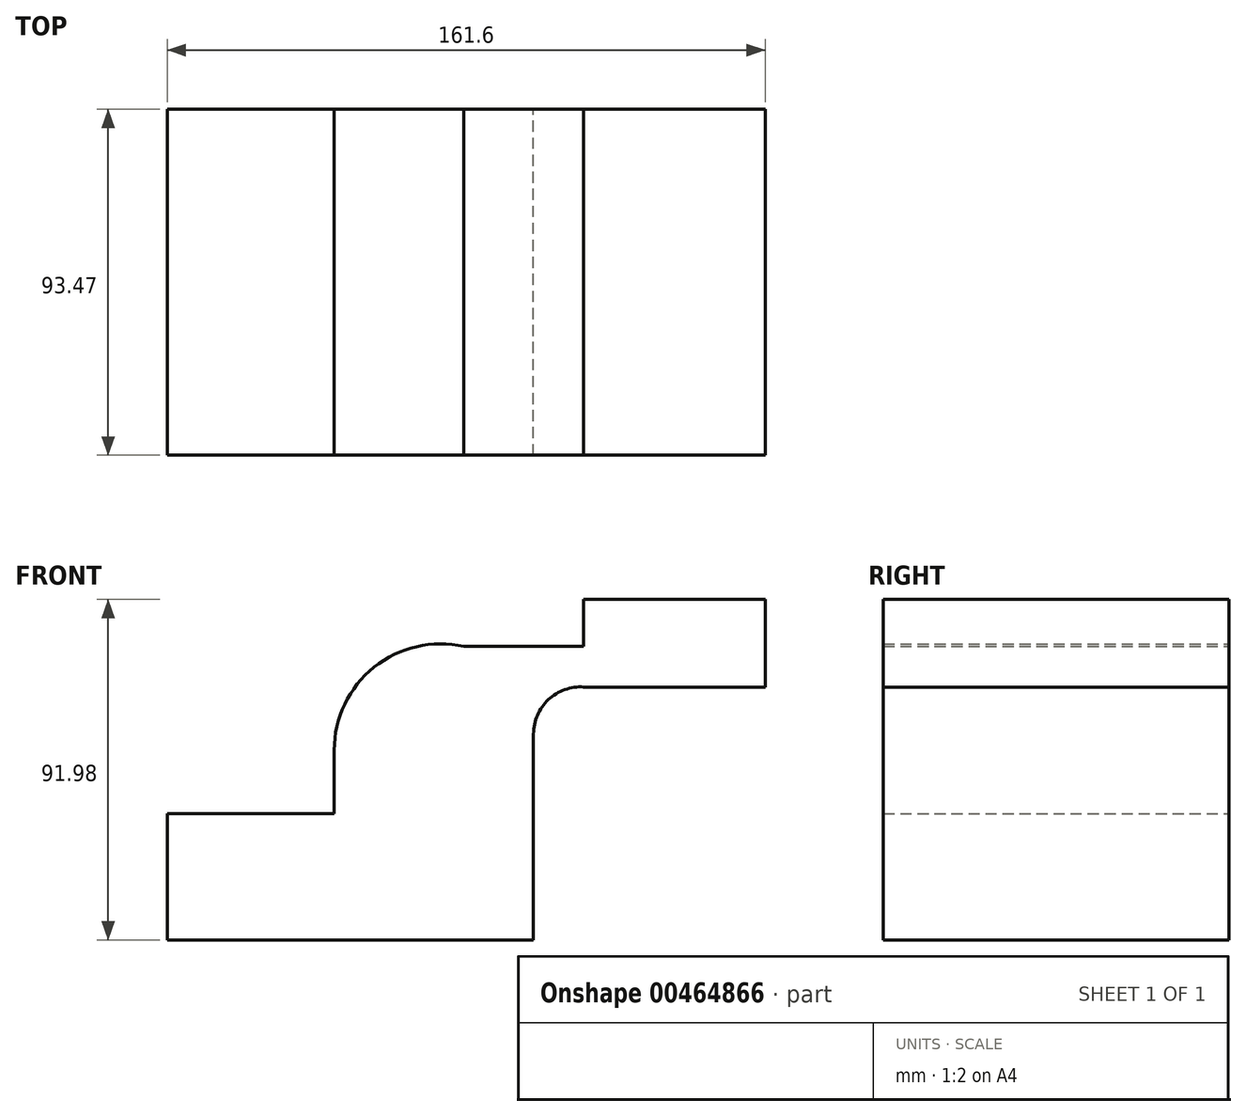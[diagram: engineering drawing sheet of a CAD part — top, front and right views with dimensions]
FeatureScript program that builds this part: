
annotation { "Feature Type Name" : "Feature", "Feature Type Description" : "" }
export const myFeature = defineFeature(function(context is Context, id is Id, definition is map)
    precondition{}
    {
        {
            var Q0;
            Q0=qCreatedBy(makeId("Front.planeOp"),FACE);
            var sketch = newSketch(context, id + "F0", { "sketchPlane" : qUnion([Q0])});
            skLineSegment(sketch, "E0.bottom", {"start": v(49.49, -17.09) * mm, "end": v(-49.49, -17.09) * mm});
            skLineSegment(sketch, "E0.top", {"start": v(49.49, 17.09) * mm, "end": v(-49.49, 17.09) * mm});
            skLineSegment(sketch, "E0.left", {"start": v(49.49, -17.09) * mm, "end": v(49.49, 17.09) * mm});
            skLineSegment(sketch, "E0.right", {"start": v(-49.49, -17.09) * mm, "end": v(-49.49, 17.09) * mm});
            skPoint(sketch, "E0.middle", {"position": v(0, 0) * mm});
            skLineSegment(sketch, "E1.bottom", {"start": v(112.11, 51.24) * mm, "end": v(63.06, 51.24) * mm});
            skLineSegment(sketch, "E1.top", {"start": v(112.11, 74.9) * mm, "end": v(63.06, 74.9) * mm});
            skLineSegment(sketch, "E1.left", {"start": v(112.11, 51.24) * mm, "end": v(112.11, 74.9) * mm});
            skLineSegment(sketch, "E1.right", {"start": v(63.06, 51.24) * mm, "end": v(63.06, 74.9) * mm});
            skPoint(sketch, "E1.middle", {"position": v(87.59, 63.07) * mm});
            skLineSegment(sketch, "E2", {"start": v(49.49, 17.09) * mm, "end": v(49.49, 38.54) * mm});
            skArc(sketch, "E3", {"start": v(49.49, 38.54) * mm, "mid": v(53.52, 47.83) * mm, "end": v(63.06, 51.24) * mm});
            skLineSegment(sketch, "E4", {"start": v(-4.38, 17.09) * mm, "end": v(-4.38, 34.16) * mm});
            skArc(sketch, "E5", {"start": v(-4.38, 34.16) * mm, "mid": v(6.4, 56.6) * mm, "end": v(30.66, 62.19) * mm});
            skLineSegment(sketch, "E6", {"start": v(30.66, 62.19) * mm, "end": v(75.1, 62.19) * mm});
            skSolve(sketch);
        }
        {
            var Q0;
            {var subQ1=sQuery(id+"F0.wireOp",EDGE,"E1.bottom");Q0=makeQuery(id+"F0.imprint","IMPRINT",FACE,{"disambiguationData":[TD([[makeQuery(id+"F0.imprint","IMPRINT",EDGE,{"derivedFrom":subQ1}),-1.0]])]});}
            var Q1;
            Q1=makeQuery(id+"F0.imprint","IMPRINT",FACE,{"disambiguationData":[TD([[makeQuery(id+"F0.imprint","IMPRINT",EDGE,{"derivedFrom":sQuery(id+"F0.wireOp",EDGE,"E0.bottom")}),-1.0]])]});
            var Q2;
            {var subQ0=sQuery(id+"F0.wireOp",EDGE,"E2");Q2=makeQuery(id+"F0.imprint","IMPRINT",FACE,{"disambiguationData":[TD([[makeQuery(id+"F0.imprint","IMPRINT",EDGE,{"derivedFrom":subQ0}),1.0]])]});}
            extrude(context, id + "F1", {"entities" : qUnion([Q0, Q1, Q2]), "depth" : 68.07 * mm});
        }
        {
            var Q0;
            Q0=makeQuery(id+"F1.opExtrude","CAP_FACE",FACE,{"disambiguationData":[OSD([sQuery(id+"F0.wireOp",EDGE,"E0.bottom"),sQuery(id+"F0.wireOp",EDGE,"E0.top"),sQuery(id+"F0.wireOp",EDGE,"E0.left"),sQuery(id+"F0.wireOp",EDGE,"E0.right"),sQuery(id+"F0.wireOp",EDGE,"E1.bottom"),sQuery(id+"F0.wireOp",EDGE,"E1.top"),sQuery(id+"F0.wireOp",EDGE,"E1.left"),sQuery(id+"F0.wireOp",EDGE,"E1.right"),sQuery(id+"F0.wireOp",EDGE,"E2"),sQuery(id+"F0.wireOp",EDGE,"E3"),sQuery(id+"F0.wireOp",EDGE,"E4"),sQuery(id+"F0.wireOp",EDGE,"E5"),sQuery(id+"F0.wireOp",EDGE,"E6")])],"isStart":false});
            extrude(context, id + "F2", {"entities" : qUnion([Q0]), "operationType" : NewBodyOperationType.ADD, "depth" : 25.4 * mm});
        }
    });
